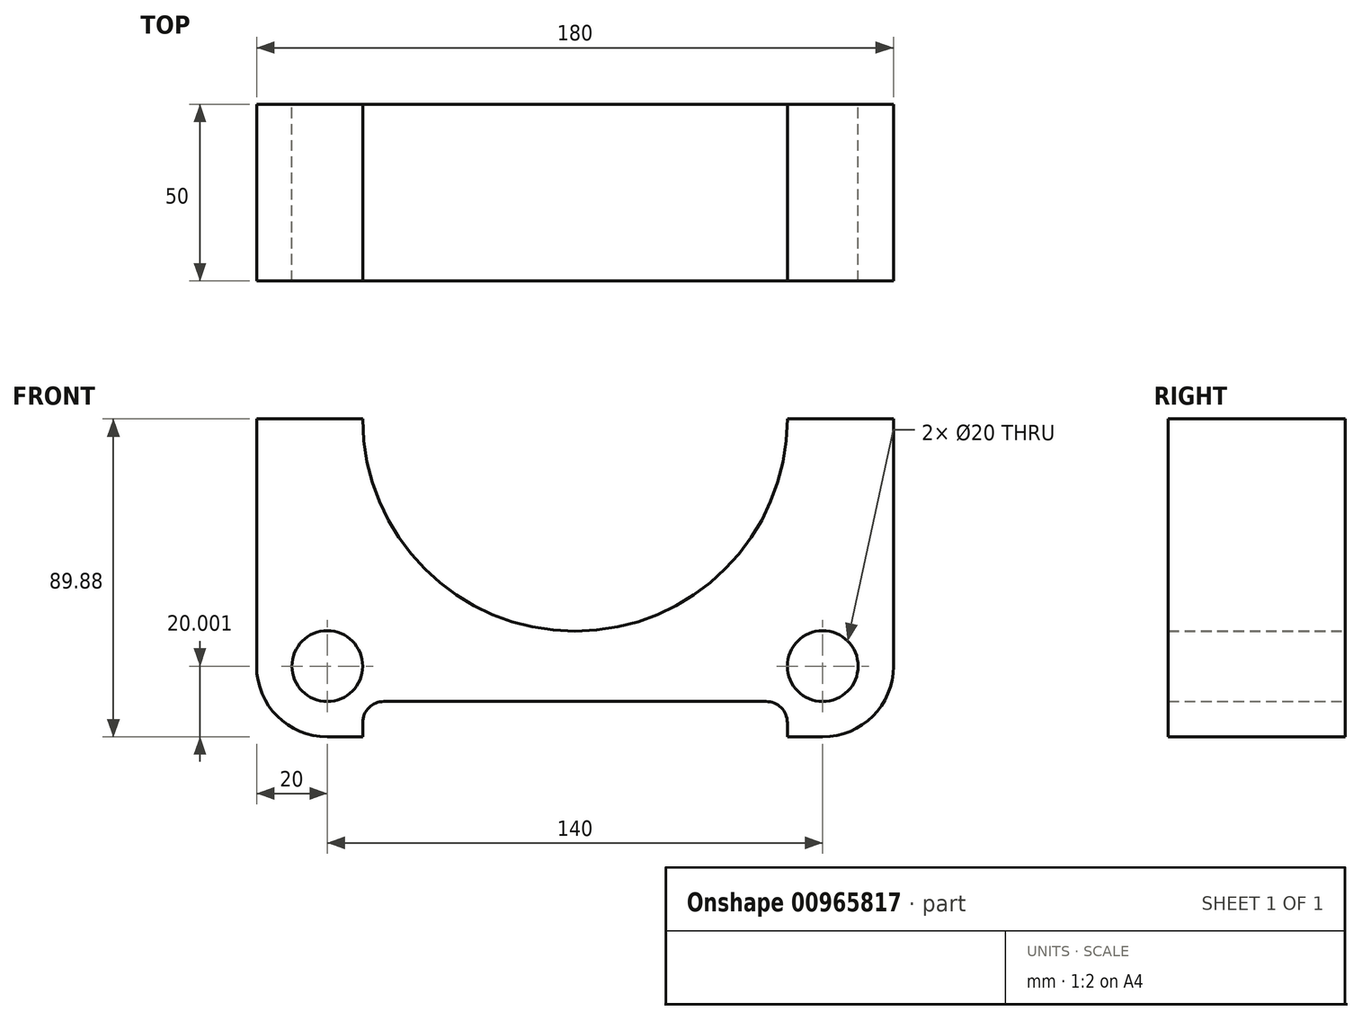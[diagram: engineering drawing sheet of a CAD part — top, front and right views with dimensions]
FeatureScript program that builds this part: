
annotation { "Feature Type Name" : "Feature", "Feature Type Description" : "" }
export const myFeature = defineFeature(function(context is Context, id is Id, definition is map)
    precondition{}
    {
        {
            var Q0;
            Q0=qCreatedBy(makeId("Front.planeOp"),FACE);
            var sketch = newSketch(context, id + "F0", { "sketchPlane" : qUnion([Q0])});
            skLineSegment(sketch, "E0", {"start": v(-90, 0) * mm, "end": v(-90, -69.88) * mm});
            skLineSegment(sketch, "E1", {"start": v(-70, -89.88) * mm, "end": v(-60, -89.88) * mm});
            skLineSegment(sketch, "E2", {"start": v(-90, 0) * mm, "end": v(-60, 0) * mm});
            skArc(sketch, "E3", {"start": v(-60, 0) * mm, "mid": v(-42.43, -42.43) * mm, "end": v(0, -60) * mm});
            skArc(sketch, "E4.MirrorCS", {"start": v(60, 0) * mm, "mid": v(42.43, -42.43) * mm, "end": v(0, -60) * mm});
            skLineSegment(sketch, "E5.MirrorCS", {"start": v(70, -89.88) * mm, "end": v(0, -89.88) * mm});
            skLineSegment(sketch, "E6.MirrorCS", {"start": v(90, 0) * mm, "end": v(90, -69.88) * mm});
            skLineSegment(sketch, "E7.MirrorCS", {"start": v(90, 0) * mm, "end": v(60, 0) * mm});
            skPoint(sketch, "E8.visualSharp", {"position": v(-90, -89.88) * mm});
            skArc(sketch, "E8.filletArc", {"start": v(-90, -69.88) * mm, "mid": v(-84.14, -84.02) * mm, "end": v(-70, -89.88) * mm});
            skPoint(sketch, "E9.visualSharp", {"position": v(90, -89.88) * mm});
            skArc(sketch, "E9.filletArc", {"start": v(70, -89.88) * mm, "mid": v(84.14, -84.02) * mm, "end": v(90, -69.88) * mm});
            skLineSegment(sketch, "E10", {"start": v(-54, -79.88) * mm, "end": v(0, -79.88) * mm});
            skLineSegment(sketch, "E11.MirrorCS", {"start": v(54, -79.88) * mm, "end": v(0, -79.88) * mm});
            skLineSegment(sketch, "E12", {"start": v(-60, -85.88) * mm, "end": v(-60, -89.88) * mm});
            skCircle(sketch, "E13", {"center": v(-70, -69.88) * mm, "radius": 10 * mm});
            skCircle(sketch, "E14.MirrorC", {"center": v(70, -69.88) * mm, "radius": 10 * mm});
            skPoint(sketch, "E15.orphan", {"position": v(-65.11, -79.88) * mm});
            skLineSegment(sketch, "E16.MirrorCS", {"start": v(60, -85.88) * mm, "end": v(60, -89.88) * mm});
            skPoint(sketch, "E17.orphan", {"position": v(-60, -93.6) * mm});
            skPoint(sketch, "E18.orphan", {"position": v(65.11, -79.88) * mm});
            skPoint(sketch, "E19.orphan", {"position": v(60, -93.6) * mm});
            skPoint(sketch, "E20.visualSharp", {"position": v(60, -79.88) * mm});
            skArc(sketch, "E20.filletArc", {"start": v(60, -85.88) * mm, "mid": v(58.24, -81.64) * mm, "end": v(54, -79.88) * mm});
            skPoint(sketch, "E21.visualSharp", {"position": v(-60, -79.88) * mm});
            skArc(sketch, "E21.filletArc", {"start": v(-54, -79.88) * mm, "mid": v(-58.24, -81.64) * mm, "end": v(-60, -85.88) * mm});
            skPoint(sketch, "E22.orphan", {"position": v(0, -89.88) * mm});
            skSolve(sketch);
        }
        {
            var Q0;
            Q0 = qSketchRegion(id + "F0", true);
            extrude(context, id + "F1", {"entities" : qUnion([Q0]), "endBound" : BoundingType.SYMMETRIC, "depth" : 50 * mm, "offsetDistance" : 25 * mm});
        }
    });
